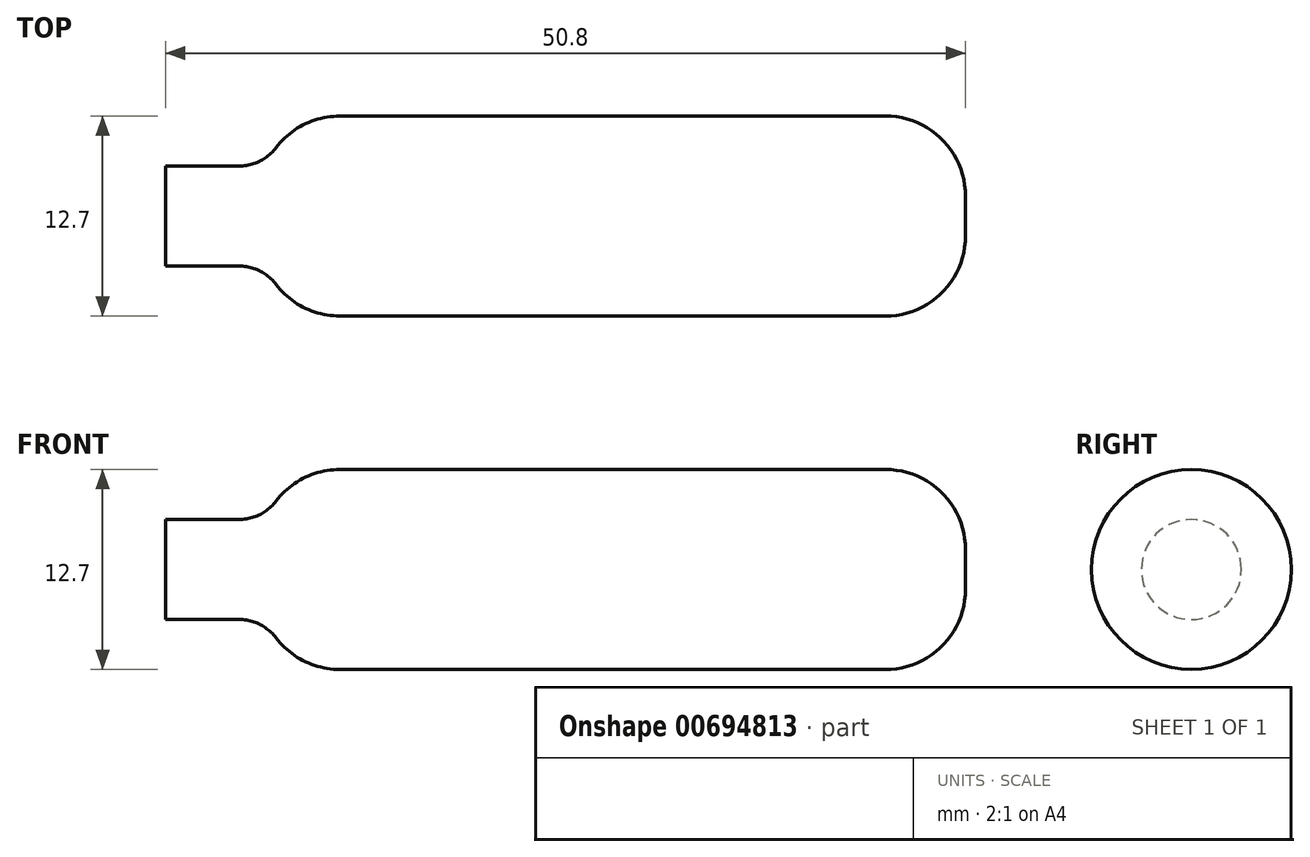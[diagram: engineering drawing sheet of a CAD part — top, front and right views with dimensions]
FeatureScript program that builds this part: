
annotation { "Feature Type Name" : "Feature", "Feature Type Description" : "" }
export const myFeature = defineFeature(function(context is Context, id is Id, definition is map)
    precondition{}
    {
        {
            var Q0;
            Q0=qCreatedBy(makeId("Right.planeOp"),FACE);
            var sketch = newSketch(context, id + "F0", { "sketchPlane" : qUnion([Q0])});
            skCircle(sketch, "E0", {"center": v(0, 0) * mm, "radius": 3.18 * mm});
            skSolve(sketch);
        }
        {
            var Q0;
            Q0 = qSketchRegion(id + "F0", true);
            extrude(context, id + "F1", {"entities" : qUnion([Q0]), "depth" : 6.35 * mm, "offsetDistance" : 25.4 * mm});
        }
        {
            var Q0;
            Q0=makeQuery(id+"F1.opExtrude","CAP_FACE",FACE,{"disambiguationData":[OSD([sQuery(id+"F0.wireOp",EDGE,"E0")])],"isStart":false});
            var sketch = newSketch(context, id + "F2", { "sketchPlane" : qUnion([Q0])});
            skCircle(sketch, "E1", {"center": v(0, 0) * mm, "radius": 6.35 * mm});
            skSolve(sketch);
        }
        {
            var Q0;
            Q0 = qSketchRegion(id + "F2", true);
            extrude(context, id + "F3", {"entities" : qUnion([Q0]), "operationType" : NewBodyOperationType.ADD, "depth" : 44.45 * mm, "offsetDistance" : 25.4 * mm});
        }
        {
            var Q0;
            Q0=makeQuery(id+"F3.opExtrude","CAP_EDGE",EDGE,{"disambiguationData":[OSD([sQuery(id+"F2.wireOp",EDGE,"E1")])],"isStart":false});
            fillet(context, id + "F4", {"entities" : qUnion([Q0]), "radius" : 5.08 * mm, "tangentPropagation" : true, "allowEdgeOverflow" : false});
        }
        {
            var Q0;
            Q0=makeQuery(id+"F3.opExtrude","CAP_EDGE",EDGE,{"disambiguationData":[OSD([sQuery(id+"F2.wireOp",EDGE,"E1")])],"isStart":true});
            fillet(context, id + "F5", {"entities" : qUnion([Q0]), "radius" : 5.08 * mm, "tangentPropagation" : true, "allowEdgeOverflow" : false});
        }
        {
            var Q0;
            Q0=makeQuery(id+"F5.opFillet","BLEND_EDGE",EDGE,{"blendedFrom":[makeQuery(id+"F3.opExtrude","CAP_EDGE",EDGE,{"disambiguationData":[OSD([sQuery(id+"F2.wireOp",EDGE,"E1")])],"isStart":true}),makeQuery(id+"F1.opExtrude","SWEPT_FACE",FACE,{"disambiguationData":[OSD([sQuery(id+"F0.wireOp",EDGE,"E0")])]})],"blendedInto":[makeQuery(id+"F1.opExtrude","SWEPT_FACE",FACE,{"disambiguationData":[OSD([sQuery(id+"F0.wireOp",EDGE,"E0")])]})]});
            fillet(context, id + "F6", {"entities" : qUnion([Q0]), "radius" : 2.96 * mm, "tangentPropagation" : true, "allowEdgeOverflow" : false});
        }
    });
